# Revit family: Domotics-DomesticRanges-GEWISS-SYSTEM_POWER-SOCKET-OUTLET_EURUSA
name_source: partatom
category: Apparecchi elettrici
revit_build: Autodesk Revit 2016 (Build: 20161004_0715(x64)
units: mm (PartAtom-declared; Revit-internal decimal feet)

## family parameters
Condiviso = Sì
Host = Superficie
Mantenere orientamento annotazione = Sì
Punto di calcolo locali = Sì
Quota connettore circolare = Usa diametro
Taglio con vuoti quando caricato = Sì
Tipo di parte = Normale

## types (2) — shared parameters
Carico apparente = 0 VA
Catalogue = DOMOTICS
Catalogue Range = SYSTEM - DOMESTIC RANGE
Description. = Euro-USA
Description: = 2P+E - 10/15A
Electrocod = 0131
For plug pins = Ã˜ 4 mm/ flat
IDF = d547b78b-161c-4cae-b9ec-3198bc792ba9
IDT = 88260a28-5918-48bb-9aa9-eb494f58f38c
Immagine tipo = GW21212.jpg
N. poli = 1
No. SYSTEM modules = 1
Produttore = GEWISS S.p.A.
Prospetto di default = 1219 mm
SEO = Socket outlet
Standard = Euro-USA
Standard: = Euro-USA
TIPO_ = System Prese EuroUsa_GENERICO : GW21212 Presa 2P+T 10/15A standard Euroamericano nero
TXT ELETTRICO = 15
Technical sheet = https://www.gewiss.com
URL = https://www.gewiss.com
Version file RFA = 19.4
Volt = 230 V
Voltage = 250/125V AC
Voltage: = 250/125V AC

## per-type parameters (varying)
| type | Colour | Descrizione | EAN code | Modello |
| GW21212 - 10/15A 2P+E euroam.socket outlet black | Black | 10/15A 2P+E EUROAM.SOCKET OUTLET SY/BK | 8011564128521 | GW21212 |
| GW20212 - 10/15A 2P+E euroam.socket outlet white | White | 10/15A 2P+E EUROAM.SOCKET OUTLET SY/WT | 8011564000650 | GW20212 |

## geometry (parser evidence)
native form markers: Sweep x2
no freeform markers — native parametric forms only
